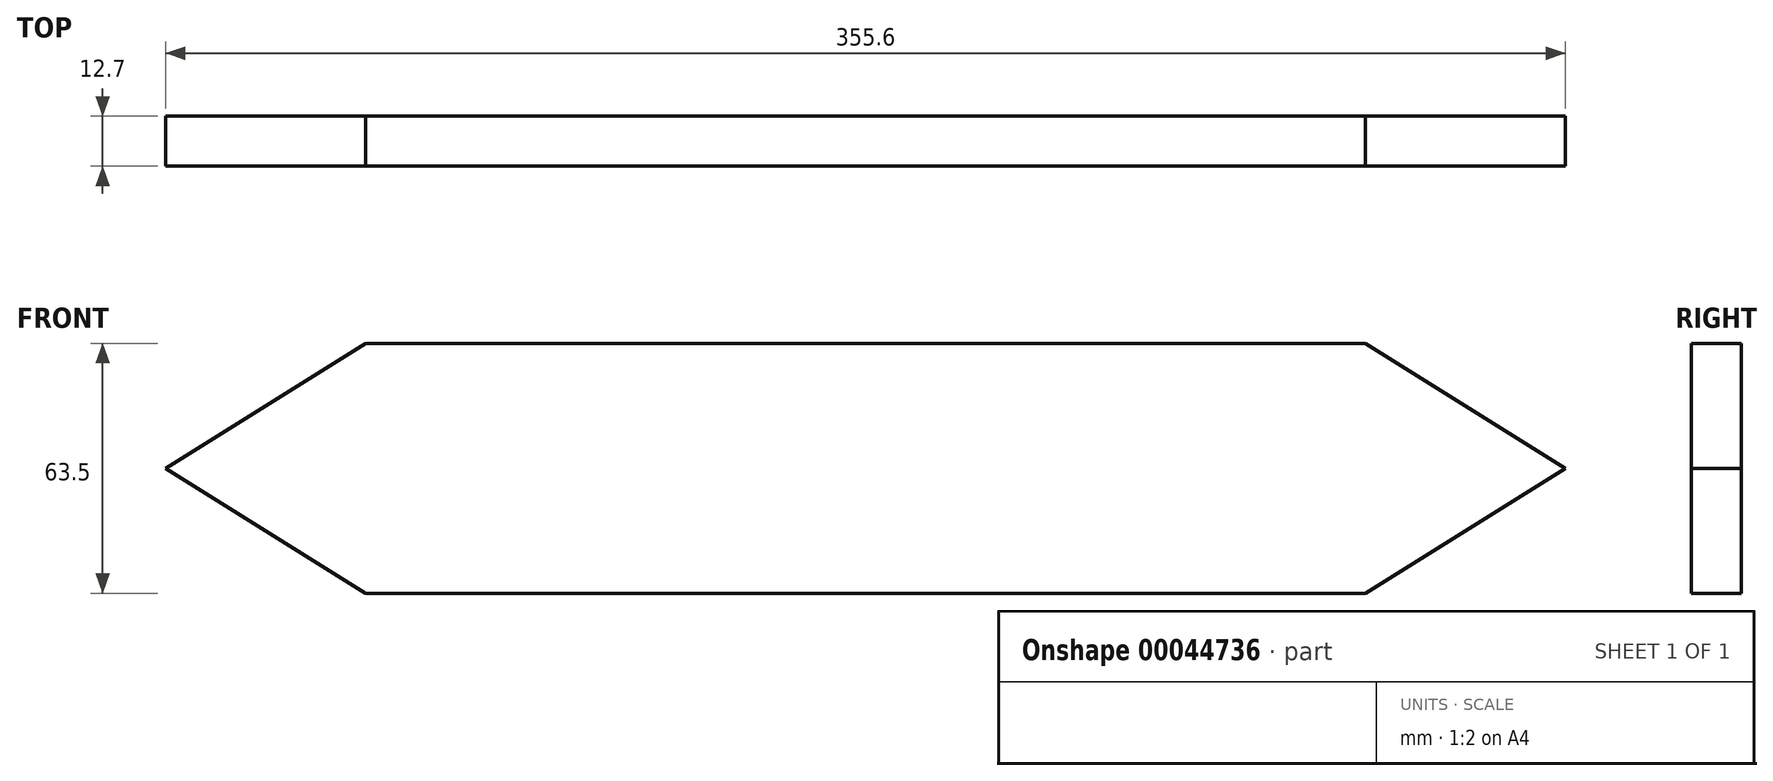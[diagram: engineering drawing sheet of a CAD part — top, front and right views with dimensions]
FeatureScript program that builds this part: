
annotation { "Feature Type Name" : "Feature", "Feature Type Description" : "" }
export const myFeature = defineFeature(function(context is Context, id is Id, definition is map)
    precondition{}
    {
        {
            var Q0;
            Q0=qCreatedBy(makeId("Front.planeOp"),FACE);
            var sketch = newSketch(context, id + "F0", { "sketchPlane" : qUnion([Q0])});
            skLineSegment(sketch, "E0.bottom", {"start": v(-162.63, -31.75) * mm, "end": v(91.37, -31.75) * mm});
            skLineSegment(sketch, "E0.top", {"start": v(-162.63, 31.75) * mm, "end": v(91.37, 31.75) * mm});
            skLineSegment(sketch, "E0.left", {"start": v(-162.63, -31.75) * mm, "end": v(-162.63, 31.75) * mm});
            skLineSegment(sketch, "E0.right", {"start": v(91.37, -31.75) * mm, "end": v(91.37, 31.75) * mm});
            skLineSegment(sketch, "E1", {"start": v(-162.63, 31.75) * mm, "end": v(-213.43, 0) * mm});
            skLineSegment(sketch, "E2", {"start": v(-213.43, 0) * mm, "end": v(-162.63, -31.75) * mm});
            skLineSegment(sketch, "E3", {"start": v(91.37, 31.75) * mm, "end": v(142.17, 0) * mm});
            skLineSegment(sketch, "E4", {"start": v(142.17, 0) * mm, "end": v(91.37, -31.75) * mm});
            skSolve(sketch);
        }
        {
            var Q0;
            Q0 = qSketchRegion(id + "F0", true);
            extrude(context, id + "F1", {"entities" : qUnion([Q0]), "depth" : 12.7 * mm});
        }
    });
